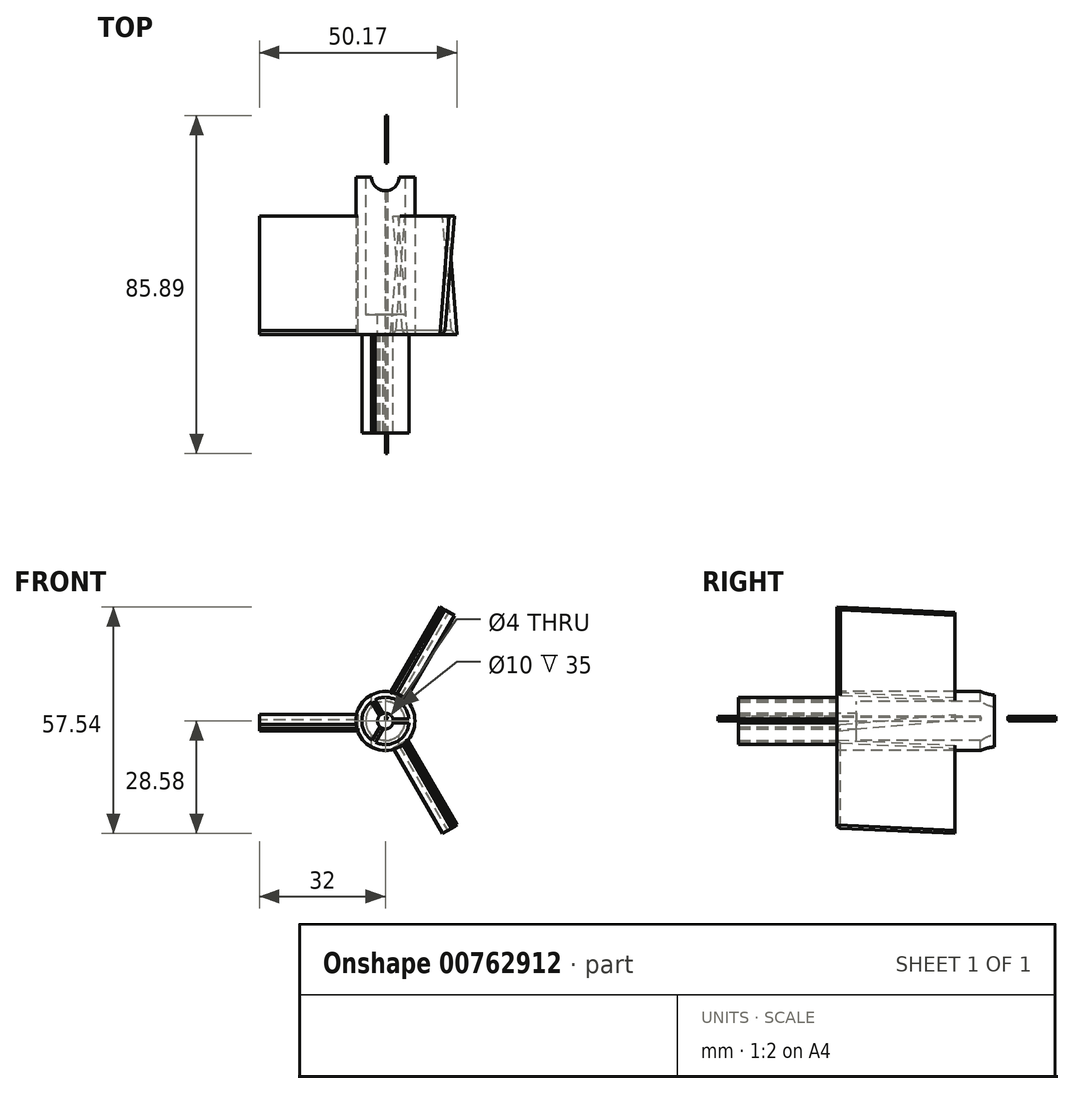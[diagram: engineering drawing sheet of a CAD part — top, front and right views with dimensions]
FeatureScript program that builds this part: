
annotation { "Feature Type Name" : "Feature", "Feature Type Description" : "" }
export const myFeature = defineFeature(function(context is Context, id is Id, definition is map)
    precondition{}
    {
        {
            var Q0;
            Q0=qCreatedBy(makeId("Front.planeOp"),FACE);
            var sketch = newSketch(context, id + "F0", { "sketchPlane" : qUnion([Q0])});
            skCircle(sketch, "E0", {"center": v(0, 0) * mm, "radius": 6 * mm});
            skCircle(sketch, "E1", {"center": v(0, 0) * mm, "radius": 7.5 * mm});
            skCircle(sketch, "E2", {"center": v(0, 0) * mm, "radius": 2 * mm});
            skCircle(sketch, "E3", {"center": v(0, 0) * mm, "radius": 5 * mm});
            skSolve(sketch);
        }
        {
            var Q0;
            Q0=makeQuery(id+"F0.imprint","IMPRINT",FACE,{"disambiguationData":[TD([[makeQuery(id+"F0.imprint","IMPRINT",EDGE,{"derivedFrom":sQuery(id+"F0.wireOp",EDGE,"E0")}),1.0]])]});
            var Q1;
            Q1=makeQuery(id+"F0.imprint","IMPRINT",FACE,{"disambiguationData":[TD([[makeQuery(id+"F0.imprint","IMPRINT",EDGE,{"derivedFrom":sQuery(id+"F0.wireOp",EDGE,"E2")}),-1.0]])]});
            extrude(context, id + "F1", {"entities" : qUnion([Q0, Q1]), "depth" : 25 * mm, "offsetDistance" : 25 * mm, "hasSecondDirection" : true, "secondDirectionOppositeDirection" : true, "secondDirectionDepth" : 5 * mm});
        }
        {
            var Q0;
            Q0=makeQuery(id+"F0.imprint","IMPRINT",FACE,{"disambiguationData":[TD([[makeQuery(id+"F0.imprint","IMPRINT",EDGE,{"derivedFrom":sQuery(id+"F0.wireOp",EDGE,"E0")}),-1.0]])]});
            var Q1;
            Q1=makeQuery(id+"F0.imprint","IMPRINT",FACE,{"disambiguationData":[TD([[makeQuery(id+"F0.imprint","IMPRINT",EDGE,{"derivedFrom":sQuery(id+"F0.wireOp",EDGE,"E0")}),1.0]])]});
            extrude(context, id + "F2", {"entities" : qUnion([Q0, Q1]), "operationType" : NewBodyOperationType.ADD, "oppositeDirection" : true, "depth" : 40 * mm, "offsetDistance" : 25 * mm});
        }
        {
            var Q0;
            Q0=qCreatedBy(makeId("Front.planeOp"),FACE);
            var sketch = newSketch(context, id + "F3", { "sketchPlane" : qUnion([Q0])});
            skLineSegment(sketch, "E4.bottom", {"start": v(0, 0.56) * mm, "end": v(7, 0.56) * mm});
            skLineSegment(sketch, "E4.top", {"start": v(0, -0.44) * mm, "end": v(7, -0.44) * mm});
            skLineSegment(sketch, "E4.left", {"start": v(0, 0.56) * mm, "end": v(0, -0.44) * mm});
            skLineSegment(sketch, "E4.right", {"start": v(7, 0.56) * mm, "end": v(7, -0.44) * mm});
            skLineSegment(sketch, "E5.1.0", {"start": v(-0.48, -0.28) * mm, "end": v(-3.98, 5.78) * mm});
            skLineSegment(sketch, "E5.1.1", {"start": v(-3.98, 5.78) * mm, "end": v(-3.12, 6.28) * mm});
            skLineSegment(sketch, "E5.1.2", {"start": v(0.38, 0.22) * mm, "end": v(-3.12, 6.28) * mm});
            skLineSegment(sketch, "E5.1.3", {"start": v(-0.48, -0.28) * mm, "end": v(0.38, 0.22) * mm});
            skLineSegment(sketch, "E5.2.0", {"start": v(0.48, -0.28) * mm, "end": v(-3.02, -6.34) * mm});
            skLineSegment(sketch, "E5.2.1", {"start": v(-3.02, -6.34) * mm, "end": v(-3.88, -5.84) * mm});
            skLineSegment(sketch, "E5.2.2", {"start": v(-0.38, 0.22) * mm, "end": v(-3.88, -5.84) * mm});
            skLineSegment(sketch, "E5.2.3", {"start": v(0.48, -0.28) * mm, "end": v(-0.38, 0.22) * mm});
            skPoint(sketch, "E5.center", {"position": v(0, 0) * mm});
            skSolve(sketch);
        }
        {
            var Q0;
            {var subQ0=sQuery(id+"F3.wireOp",EDGE,"E5.1.1");Q0=makeQuery(id+"F3.imprint","IMPRINT",FACE,{"disambiguationData":[TD([[makeQuery(id+"F3.imprint","IMPRINT",EDGE,{"derivedFrom":subQ0}),-1.0]])]});}
            var Q1;
            {var subQ5=sQuery(id+"F3.wireOp",EDGE,"E4.right");Q1=makeQuery(id+"F3.imprint","IMPRINT",FACE,{"disambiguationData":[TD([[makeQuery(id+"F3.imprint","IMPRINT",EDGE,{"derivedFrom":subQ5}),-1.0]])]});}
            var Q2;
            {var subQ5=sQuery(id+"F3.wireOp",EDGE,"E5.2.1");Q2=makeQuery(id+"F3.imprint","IMPRINT",FACE,{"disambiguationData":[TD([[makeQuery(id+"F3.imprint","IMPRINT",EDGE,{"derivedFrom":subQ5}),-1.0]])]});}
            extrude(context, id + "F4", {"entities" : qUnion([Q0, Q1, Q2]), "operationType" : NewBodyOperationType.REMOVE, "depth" : 25 * mm, "offsetDistance" : 25 * mm});
        }
        {
            var Q0;
            Q0=qCreatedBy(makeId("Front.planeOp"),FACE);
            var sketch = newSketch(context, id + "F5", { "sketchPlane" : qUnion([Q0])});
            skLineSegment(sketch, "E6.bottom", {"start": v(-7, -1) * mm, "end": v(-32, -1) * mm});
            skLineSegment(sketch, "E6.top", {"start": v(-7, -2.5) * mm, "end": v(-32, -2.5) * mm});
            skLineSegment(sketch, "E6.left", {"start": v(-7, -1) * mm, "end": v(-7, -2.5) * mm});
            skLineSegment(sketch, "E6.right", {"start": v(-32, -1) * mm, "end": v(-32, -2.5) * mm});
            skSolve(sketch);
        }
        {
            var Q0;
            Q0=qCreatedBy(makeId("Right.planeOp"),FACE);
            var sketch = newSketch(context, id + "F6", { "sketchPlane" : qUnion([Q0])});
            skLineSegment(sketch, "E7", {"start": v(0, -1.71) * mm, "end": v(30, 1.01) * mm});
            skSolve(sketch);
        }
        {
            var Q0;
            Q0=makeQuery(id+"F5.imprint","IMPRINT",FACE,{"disambiguationData":[TD([[makeQuery(id+"F5.imprint","IMPRINT",EDGE,{"derivedFrom":sQuery(id+"F5.wireOp",EDGE,"E6.bottom")}),1.0]])]});
            var Q1;
            Q1=sQuery(id+"F6.wireOp",EDGE,"E7");
            sweep(context, id + "F7", {"profiles" : qUnion([Q0]), "path" : qUnion([Q1])});
        }
        {
            var Q0;
            Q0=qCreatedBy(makeId("Right.planeOp"),FACE);
            var sketch = newSketch(context, id + "F8", { "sketchPlane" : qUnion([Q0])});
            skLineSegment(sketch, "E8", {"start": v(-30.2, 0) * mm, "end": v(55.62, 0) * mm});
            skLineSegment(sketch, "E9", {"start": v(55.62, 0) * mm, "end": v(55.62, 1.11) * mm});
            skLineSegment(sketch, "E10", {"start": v(55.62, 1.11) * mm, "end": v(-30.27, 1.11) * mm});
            skLineSegment(sketch, "E11", {"start": v(-30.27, 1.11) * mm, "end": v(-30.2, 0) * mm});
            skSolve(sketch);
        }
        {
            var Q0;
            Q0=makeQuery(id+"F7.opSweep","CAP_EDGE",EDGE,{"disambiguationData":[OSD([sQuery(id+"F5.wireOp",EDGE,"E6.bottom"),sQuery(id+"F6.wireOp",VERTEX,"E7.start")])],"isStart":true});
            chamfer(context, id + "F9", {"entities" : qUnion([Q0]), "width" : 1 * mm, "tangentPropagation" : true});
        }
        {
            var Q0;
            Q0=makeQuery(id+"F8.imprint","IMPRINT",FACE,{"disambiguationData":[TD([[makeQuery(id+"F8.imprint","IMPRINT",EDGE,{"derivedFrom":sQuery(id+"F8.wireOp",EDGE,"E8")}),1.0]])]});
            var Q1;
            Q1=sQuery(id+"F8.wireOp",EDGE,"E8");
            revolve(context, id + "F10", {"surfaceOperationType" : NewSurfaceOperationType.NEW, "entities" : qUnion([Q0]), "axis" : qUnion([Q1]), "revolveType" : RevolveType.ONE_DIRECTION, "angle" : 30 * degree});
        }
        {
            var Q0;
            Q0=makeQuery(id+"F7.opSweep","SWEPT_BODY",BODY,{"disambiguationData":[OSD([sQuery(id+"F5.wireOp",EDGE,"E6.bottom"),sQuery(id+"F5.wireOp",EDGE,"E6.top"),sQuery(id+"F5.wireOp",EDGE,"E6.left"),sQuery(id+"F5.wireOp",EDGE,"E6.right"),sQuery(id+"F6.wireOp",EDGE,"E7")])]});
            var Q1;
            Q1=makeQuery(id+"F10.opRevolve","CAP_EDGE",EDGE,{"disambiguationData":[OSD([sQuery(id+"F8.wireOp",EDGE,"E8")])],"isStart":true});
            circularPattern(context, id + "F11", {"entities" : qUnion([Q0]), "axis" : qUnion([Q1]), "angle" : 360 * degree, "instanceCount" : 3, "equalSpace" : true});
        }
        {
            var Q0;
            Q0=qCreatedBy(makeId("Top.planeOp"),FACE);
            var sketch = newSketch(context, id + "F12", { "sketchPlane" : qUnion([Q0])});
            skCircle(sketch, "E12", {"center": v(0, 40) * mm, "radius": 3.5 * mm});
            skSolve(sketch);
        }
        {
            var Q0;
            Q0 = qSketchRegion(id + "F12", true);
            extrude(context, id + "F13", {"entities" : qUnion([Q0]), "operationType" : NewBodyOperationType.REMOVE, "oppositeDirection" : true, "depth" : 25 * mm, "offsetDistance" : 25 * mm, "hasSecondDirection" : true, "secondDirectionOppositeDirection" : false, "secondDirectionDepth" : 25 * mm});
        }
    });
